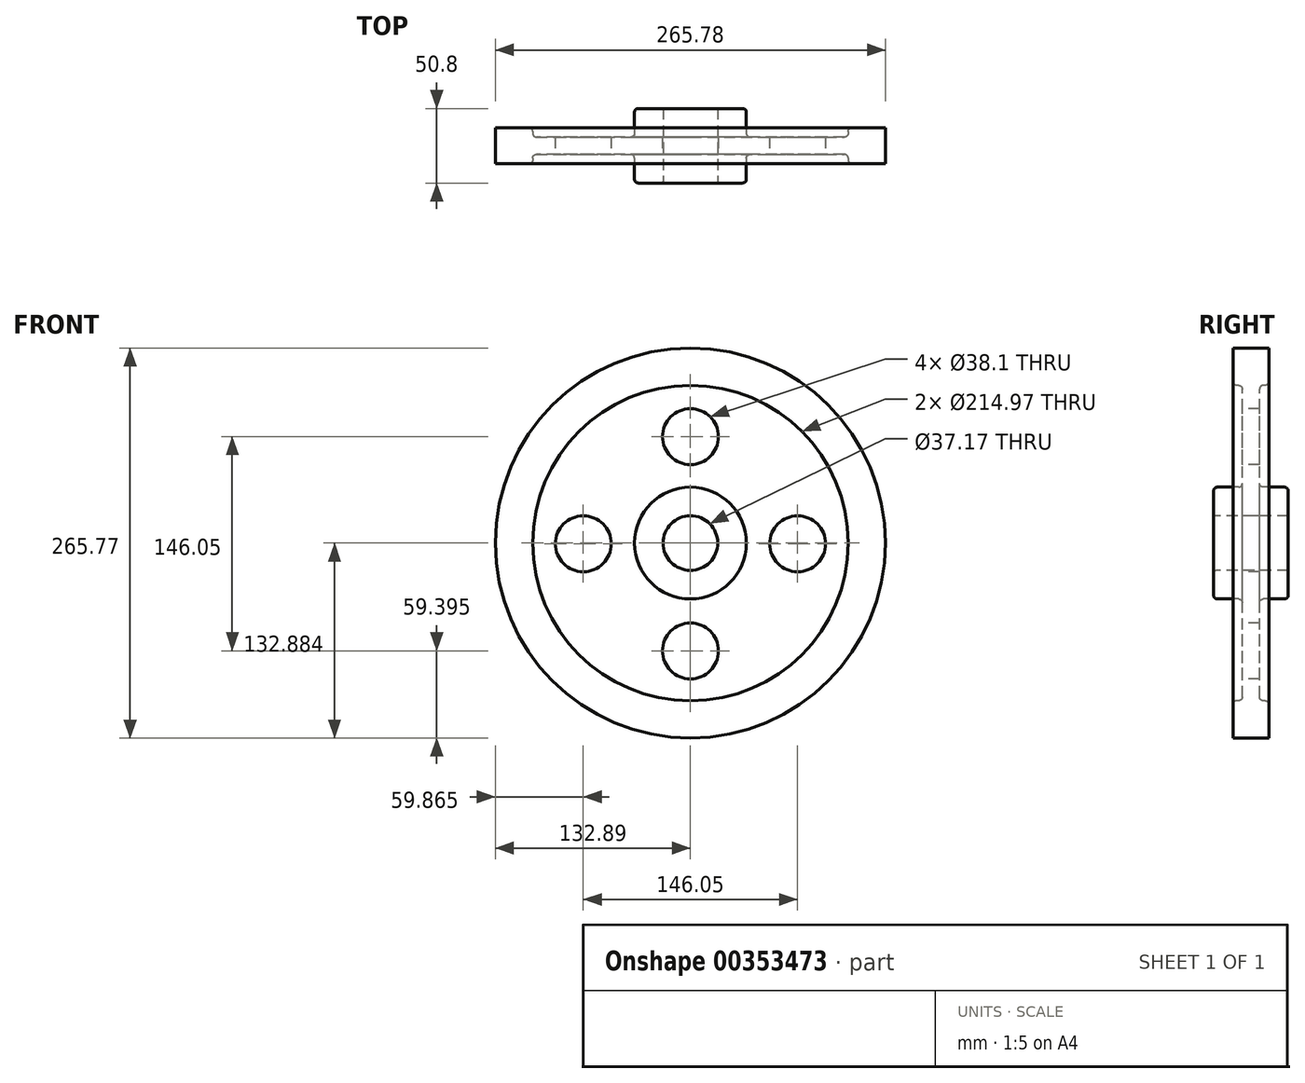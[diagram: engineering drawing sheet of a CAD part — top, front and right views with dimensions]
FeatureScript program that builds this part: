
annotation { "Feature Type Name" : "Feature", "Feature Type Description" : "" }
export const myFeature = defineFeature(function(context is Context, id is Id, definition is map)
    precondition{}
    {
        {
            var Q0;
            Q0=qCreatedBy(makeId("Right.planeOp"),FACE);
            var sketch = newSketch(context, id + "F0", { "sketchPlane" : qUnion([Q0])});
            skLineSegment(sketch, "E0", {"start": v(0, 0) * mm, "end": v(6.35, 0) * mm});
            skLineSegment(sketch, "E1.0", {"start": v(0, 19.05) * mm, "end": v(25.86, 19.05) * mm});
            skLineSegment(sketch, "E2.0", {"start": v(0, 133.35) * mm, "end": v(12.7, 133.35) * mm});
            skLineSegment(sketch, "E3", {"start": v(0, 0) * mm, "end": v(0, 133.35) * mm});
            skLineSegment(sketch, "E4.2", {"start": v(0.46, 0.46) * mm, "end": v(99.56, 0.46) * mm});
            skLineSegment(sketch, "E5.0", {"start": v(25.86, 19.05) * mm, "end": v(25.86, 38.56) * mm});
            skLineSegment(sketch, "E6.trimOffspring", {"start": v(12.7, 132.89) * mm, "end": v(12.7, 133.35) * mm});
            skLineSegment(sketch, "E7.trimOffspring", {"start": v(6.35, 38.56) * mm, "end": v(6.35, 107.95) * mm});
            skLineSegment(sketch, "E8", {"start": v(12.7, 132.89) * mm, "end": v(12.7, 107.95) * mm});
            skLineSegment(sketch, "E9", {"start": v(6.35, 107.95) * mm, "end": v(12.7, 107.95) * mm});
            skLineSegment(sketch, "E10.trimOffspring", {"start": v(6.35, 38.56) * mm, "end": v(25.86, 38.56) * mm});
            skLineSegment(sketch, "E11.trimOffspring", {"start": v(12.7, 0) * mm, "end": v(99.56, 0) * mm});
            skLineSegment(sketch, "E12.MirrorCS", {"start": v(-11.77, 132.89) * mm, "end": v(-11.77, 107.95) * mm});
            skLineSegment(sketch, "E13.MirrorCS", {"start": v(0.93, 133.35) * mm, "end": v(-11.77, 133.35) * mm});
            skLineSegment(sketch, "E14.MirrorCS", {"start": v(-5.42, 107.95) * mm, "end": v(-11.77, 107.95) * mm});
            skLineSegment(sketch, "E15.MirrorCS", {"start": v(-5.42, 38.56) * mm, "end": v(-5.42, 107.95) * mm});
            skLineSegment(sketch, "E16.MirrorCS", {"start": v(-5.42, 38.56) * mm, "end": v(-24.94, 38.56) * mm});
            skLineSegment(sketch, "E17.MirrorCS", {"start": v(-24.94, 19.05) * mm, "end": v(-24.94, 38.56) * mm});
            skLineSegment(sketch, "E18.MirrorCS", {"start": v(0.93, 19.05) * mm, "end": v(-24.94, 19.05) * mm});
            skLineSegment(sketch, "E19", {"start": v(-11.77, 133.35) * mm, "end": v(-11.77, 132.89) * mm});
            skSolve(sketch);
        }
        {
            var Q0;
            Q0=makeQuery(id+"F0.imprint","IMPRINT",FACE,{"disambiguationData":[TD([[makeQuery(id+"F0.imprint","IMPRINT",EDGE,{"derivedFrom":sQuery(id+"F0.wireOp",EDGE,"E12.MirrorCS")}),1.0]])]});
            var Q1;
            {var subQ4=sQuery(id+"F0.wireOp",EDGE,"E1.0");Q1=makeQuery(id+"F0.imprint","IMPRINT",FACE,{"disambiguationData":[TD([[makeQuery(id+"F0.imprint","IMPRINT",EDGE,{"derivedFrom":subQ4}),1.0]])]});}
            var Q2;
            Q2=sQuery(id+"F0.wireOp",EDGE,"E4.2");
            revolve(context, id + "F1", {"entities" : qUnion([Q0, Q1]), "axis" : qUnion([Q2]), "revolveType" : RevolveType.FULL});
        }
        {
            var Q0;
            Q0=makeQuery(id+"F1.opRevolve","SWEPT_FACE",FACE,{"disambiguationData":[OSD([sQuery(id+"F0.wireOp",EDGE,"E15.MirrorCS")])]});
            var sketch = newSketch(context, id + "F2", { "sketchPlane" : qUnion([Q0])});
            skLineSegment(sketch, "E20", {"start": v(0, 0) * mm, "end": v(0, 73.03) * mm});
            skCircle(sketch, "E21", {"center": v(0, 73.03) * mm, "radius": 19.05 * mm});
            skCircle(sketch, "E22.1.0", {"center": v(-73.03, 0) * mm, "radius": 19.05 * mm});
            skCircle(sketch, "E22.2.0", {"center": v(0, -73.03) * mm, "radius": 19.05 * mm});
            skCircle(sketch, "E22.3.0", {"center": v(73.03, 0) * mm, "radius": 19.05 * mm});
            skPoint(sketch, "E22.center", {"position": v(0, 0) * mm});
            skSolve(sketch);
        }
        {
            var Q0;
            Q0=makeQuery(id+"F2.imprint","IMPRINT",FACE,{"disambiguationData":[TD([[makeQuery(id+"F2.imprint","IMPRINT",EDGE,{"derivedFrom":sQuery(id+"F2.wireOp",EDGE,"E21")}),1.0]])]});
            var Q1;
            Q1=makeQuery(id+"F2.imprint","IMPRINT",FACE,{"disambiguationData":[TD([[makeQuery(id+"F2.imprint","IMPRINT",EDGE,{"derivedFrom":sQuery(id+"F2.wireOp",EDGE,"E22.1.0")}),1.0]])]});
            var Q2;
            Q2=makeQuery(id+"F2.imprint","IMPRINT",FACE,{"disambiguationData":[TD([[makeQuery(id+"F2.imprint","IMPRINT",EDGE,{"derivedFrom":sQuery(id+"F2.wireOp",EDGE,"E22.3.0")}),1.0]])]});
            var Q3;
            Q3=makeQuery(id+"F2.imprint","IMPRINT",FACE,{"disambiguationData":[TD([[makeQuery(id+"F2.imprint","IMPRINT",EDGE,{"derivedFrom":sQuery(id+"F2.wireOp",EDGE,"E22.2.0")}),1.0]])]});
            extrude(context, id + "F3", {"entities" : qUnion([Q0, Q1, Q2, Q3]), "operationType" : NewBodyOperationType.REMOVE, "oppositeDirection" : true, "depth" : 25.4 * mm});
        }
        {
            var Q0;
            Q0=makeQuery(id+"F1.opRevolve","SWEPT_EDGE",EDGE,{"disambiguationData":[OSD([sQuery(id+"F0.wireOp",EDGE,"E12.MirrorCS"),sQuery(id+"F0.wireOp",EDGE,"E14.MirrorCS")])]});
            var Q1;
            Q1=makeQuery(id+"F1.opRevolve","SWEPT_EDGE",EDGE,{"disambiguationData":[OSD([sQuery(id+"F0.wireOp",EDGE,"E14.MirrorCS"),sQuery(id+"F0.wireOp",EDGE,"E15.MirrorCS")])]});
            var Q2;
            Q2=makeQuery(id+"F1.opRevolve","SWEPT_EDGE",EDGE,{"disambiguationData":[OSD([sQuery(id+"F0.wireOp",EDGE,"E16.MirrorCS"),sQuery(id+"F0.wireOp",EDGE,"E17.MirrorCS")])]});
            var Q3;
            Q3=makeQuery(id+"F1.opRevolve","SWEPT_EDGE",EDGE,{"disambiguationData":[OSD([sQuery(id+"F0.wireOp",EDGE,"E15.MirrorCS"),sQuery(id+"F0.wireOp",EDGE,"E16.MirrorCS")])]});
            fillet(context, id + "F4", {"entities" : qUnion([Q0, Q1, Q2, Q3]), "radius" : 2.54 * mm, "tangentPropagation" : true, "allowEdgeOverflow" : false});
        }
        {
            var Q0;
            Q0=makeQuery(id+"F1.opRevolve","SWEPT_EDGE",EDGE,{"disambiguationData":[OSD([sQuery(id+"F0.wireOp",EDGE,"E17.MirrorCS"),sQuery(id+"F0.wireOp",EDGE,"E18.MirrorCS")])]});
            fillet(context, id + "F5", {"entities" : qUnion([Q0]), "radius" : 1.59 * mm, "tangentPropagation" : true, "allowEdgeOverflow" : false});
        }
        {
            var Q0;
            Q0=makeQuery(id+"F1.opRevolve","SWEPT_EDGE",EDGE,{"disambiguationData":[OSD([sQuery(id+"F0.wireOp",EDGE,"E7.trimOffspring"),sQuery(id+"F0.wireOp",EDGE,"E10.trimOffspring")])]});
            var Q1;
            Q1=makeQuery(id+"F1.opRevolve","SWEPT_EDGE",EDGE,{"disambiguationData":[OSD([sQuery(id+"F0.wireOp",EDGE,"E5.0"),sQuery(id+"F0.wireOp",EDGE,"E10.trimOffspring")])]});
            var Q2;
            Q2=makeQuery(id+"F1.opRevolve","SWEPT_EDGE",EDGE,{"disambiguationData":[OSD([sQuery(id+"F0.wireOp",EDGE,"E8"),sQuery(id+"F0.wireOp",EDGE,"E9")])]});
            var Q3;
            Q3=makeQuery(id+"F1.opRevolve","SWEPT_EDGE",EDGE,{"disambiguationData":[OSD([sQuery(id+"F0.wireOp",EDGE,"E7.trimOffspring"),sQuery(id+"F0.wireOp",EDGE,"E9")])]});
            fillet(context, id + "F6", {"entities" : qUnion([Q0, Q1, Q2, Q3]), "radius" : 2.54 * mm, "tangentPropagation" : true, "allowEdgeOverflow" : false});
        }
    });
